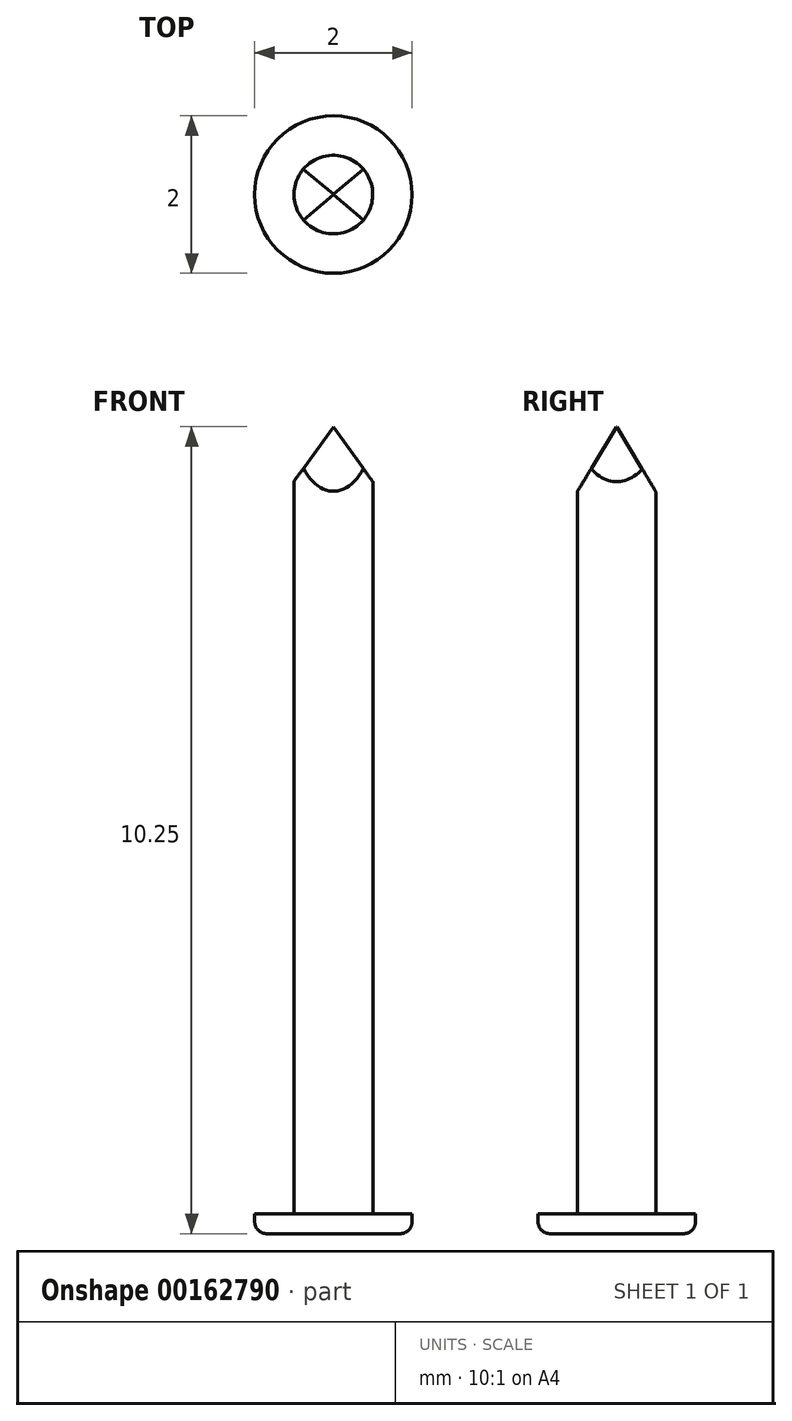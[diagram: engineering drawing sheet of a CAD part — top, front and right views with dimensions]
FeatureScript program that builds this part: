
annotation { "Feature Type Name" : "Feature", "Feature Type Description" : "" }
export const myFeature = defineFeature(function(context is Context, id is Id, definition is map)
    precondition{}
    {
        {
            var Q0;
            Q0=qCreatedBy(makeId("Top.planeOp"),FACE);
            var sketch = newSketch(context, id + "F0", { "sketchPlane" : qUnion([Q0])});
            skCircle(sketch, "E0", {"center": v(0, 0) * mm, "radius": 0.5 * mm});
            skCircle(sketch, "E1", {"center": v(0, 0) * mm, "radius": 1 * mm});
            skSolve(sketch);
        }
        {
            var Q0;
            Q0=makeQuery(id+"F0.imprint","IMPRINT",FACE,{"disambiguationData":[TD([[makeQuery(id+"F0.imprint","IMPRINT",EDGE,{"derivedFrom":sQuery(id+"F0.wireOp",EDGE,"E0")}),1.0]])]});
            extrude(context, id + "F1", {"entities" : qUnion([Q0]), "depth" : 10 * mm});
        }
        {
            var Q0;
            Q0=makeQuery(id+"F0.imprint","IMPRINT",FACE,{"disambiguationData":[TD([[makeQuery(id+"F0.imprint","IMPRINT",EDGE,{"derivedFrom":sQuery(id+"F0.wireOp",EDGE,"E0")}),1.0]])]});
            var Q1;
            Q1=makeQuery(id+"F0.imprint","IMPRINT",FACE,{"disambiguationData":[TD([[makeQuery(id+"F0.imprint","IMPRINT",EDGE,{"derivedFrom":sQuery(id+"F0.wireOp",EDGE,"E0")}),-1.0]])]});
            var Q2;
            Q2=sQuery(id+"F0.wireOp",EDGE,"E0");
            var Q3;
            Q3=sQuery(id+"F0.wireOp",EDGE,"E1");
            extrude(context, id + "F2", {"entities" : qUnion([Q0, Q1]), "operationType" : NewBodyOperationType.ADD, "surfaceEntities" : qUnion([Q2, Q3]), "oppositeDirection" : true, "depth" : 0.25 * mm});
        }
        {
            var Q0;
            Q0=makeQuery(id+"F2.opExtrude","CAP_EDGE",EDGE,{"disambiguationData":[OSD([sQuery(id+"F0.wireOp",EDGE,"E1")])],"isStart":false});
            fillet(context, id + "F3", {"entities" : qUnion([Q0]), "radius" : .15 * mm, "tangentPropagation" : true, "allowEdgeOverflow" : false});
        }
        {
            var Q0;
            Q0=qCreatedBy(makeId("Right.planeOp"),FACE);
            var sketch = newSketch(context, id + "F4", { "sketchPlane" : qUnion([Q0])});
            skLineSegment(sketch, "E2", {"start": v(0, 10) * mm, "end": v(0.58, 9.03) * mm});
            skLineSegment(sketch, "E3", {"start": v(0.58, 9.03) * mm, "end": v(0.58, 10.09) * mm});
            skLineSegment(sketch, "E4", {"start": v(0.58, 10.09) * mm, "end": v(-0.65, 10.09) * mm});
            skLineSegment(sketch, "E5", {"start": v(-0.65, 10.09) * mm, "end": v(-0.57, 9.06) * mm});
            skLineSegment(sketch, "E6", {"start": v(-0.57, 9.06) * mm, "end": v(0, 10) * mm});
            skSolve(sketch);
        }
        {
            var Q0;
            Q0=makeQuery(id+"F4.imprint","IMPRINT",FACE,{"disambiguationData":[TD([[makeQuery(id+"F4.imprint","IMPRINT",EDGE,{"derivedFrom":sQuery(id+"F4.wireOp",EDGE,"E2")}),1.0]])]});
            extrude(context, id + "F5", {"entities" : qUnion([Q0]), "operationType" : NewBodyOperationType.REMOVE, "depth" : 25 * mm, "hasSecondDirection" : true, "secondDirectionOppositeDirection" : true, "secondDirectionDepth" : 25 * mm});
        }
        {
            var Q0;
            Q0=qCreatedBy(makeId("Front.planeOp"),FACE);
            var sketch = newSketch(context, id + "F6", { "sketchPlane" : qUnion([Q0])});
            skLineSegment(sketch, "E7", {"start": v(0, 10) * mm, "end": v(-0.6, 9.18) * mm});
            skLineSegment(sketch, "E8", {"start": v(-0.6, 9.18) * mm, "end": v(-0.6, 10.3) * mm});
            skLineSegment(sketch, "E9", {"start": v(-0.6, 10.3) * mm, "end": v(0.64, 10.3) * mm});
            skLineSegment(sketch, "E10", {"start": v(0.64, 10.3) * mm, "end": v(0.58, 9.2) * mm});
            skLineSegment(sketch, "E11", {"start": v(0.58, 9.2) * mm, "end": v(0, 10) * mm});
            skSolve(sketch);
        }
        {
            var Q0;
            Q0=makeQuery(id+"F6.imprint","IMPRINT",FACE,{"disambiguationData":[TD([[makeQuery(id+"F6.imprint","IMPRINT",EDGE,{"derivedFrom":sQuery(id+"F6.wireOp",EDGE,"E7")}),-1.0]])]});
            extrude(context, id + "F7", {"entities" : qUnion([Q0]), "operationType" : NewBodyOperationType.REMOVE, "depth" : 25 * mm, "hasSecondDirection" : true, "secondDirectionOppositeDirection" : true, "secondDirectionDepth" : 25 * mm});
        }
    });
